# Revit family: Accessories_Set-Grohe-Essentials_Cube_Master-40778_Series
name_source: partatom
category: Specialty Equipment
units: mm (PartAtom-declared; Revit-internal decimal feet)

## family parameters
Cut with Voids When Loaded = No
Host = Face
OmniClass Number = 23.40.20.21
OmniClass Title = Toilet and Bath Specialties
Part Type = Normal
Room Calculation Point = No
Round Connector Dimension = Use Diameter
Shared = Yes

## types (3) — shared parameters
Assembly Code = C1030200
Default Elevation = 16"
Description = Essentials 4-in-1 Accessory Set
Height = 5"
Installation Type = Wall Mounted
Length = 2 3/8"
Manufacturer = Grohe
Product Documentation Link = https://americanstandard.box.com
Product Page URL = https://www.grohe.us
Revised Date = 06/07/2023
Robe Hook 40511 = No
Toilet Paper Holder 40507 = Yes
Towel Bar 40509 = No
Towel Ring 40510 = No
URL = https://www.grohe.us
Width = 23 5/8"

## per-type parameters (varying)
| type | Finish | Material |
| 40778001 | Metal-Grohe-001-StarLight Chrome | Metal-Grohe-001-StarLight Chrome |
| 407782431 | Metal-Grohe-2431-Matte Black | Metal-Grohe-2431-Matte Black |
| 40778GN1 | Metal-Grohe-GN1-Brushed Cool Sunrise | Metal-Grohe-GN1-Brushed Cool Sunrise |

note: column(s) folded — value = type name in every type: Model

## geometry (parser evidence)
native form markers: Sweep x4
no freeform markers — native parametric forms only
